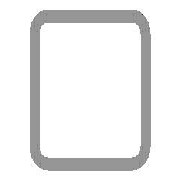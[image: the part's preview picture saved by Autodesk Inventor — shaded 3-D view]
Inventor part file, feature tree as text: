
AUTODESK INVENTOR PART (.ipt)
format: ipt  version: 2025.3 (Build 293356030, 356C)  size: 158,208 bytes
history: native  units: mm (DEFAULTED — no unit token found)
features: other x4, plane x3, split x2, sketch x1
ambient origin geometry x8: Origin, YZ Plane, XZ Plane, XY Plane, X Axis, Y Axis, Z Axis, Center Point
bodies: Solid1 (feature_tree), Body (feature_tree)
feature tree (10):
  parser-record x1  (decoder bookkeeping rows leaked as tree rows — omitted from the tree; the rows remain in map.json)
  other  "Driven Length"
  other  "Start plane"
  other  "End plane"
  plane  "Work Plane4"
  split  "Split1"
  plane  "Work Plane5"
  split  "Split2"
  sketch  "Sketch3"  dims[d3=2986.24836mm d4=0.0mm d7=6.0mm d9=60.0mm d11=60.0mm d12=3.0mm d13=133.333333mm d14=3119.581693mm d15=30.0mm d16=30.0mm d17=90.0deg d18=2986.24836mm]
  plane  "Work Plane3"
